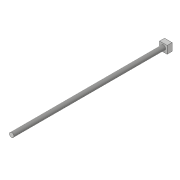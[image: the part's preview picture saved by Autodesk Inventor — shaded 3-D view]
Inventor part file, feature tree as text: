
AUTODESK INVENTOR PART (.ipt)
format: ipt  version: 2019 (Build 230136000, 136)  size: 96,256 bytes
history: native  units: in
note: dims shown in document units (in); Inventor stores cm internally (conversion verified against a paired STEP export)
features: extrude x3, sketch x3, thread x2, plane x1
ambient origin geometry x8: Origin, YZ Plane, XZ Plane, XY Plane, X Axis, Y Axis, Z Axis, Center Point
bodies: Solid1 (feature_tree)
feature tree (9):
  extrude  "Extrusion1"  Depth=0.5906in
  extrude  "Extrusion2"  Depth=0.3937in TaperAngle=0.0deg
  thread  "Thread1"  [1 undecoded]
  plane  "Work Plane1"
  extrude  "Extrusion3"  Depth=0.3937in
  thread  "Thread2"  [1 undecoded]
  sketch  "Sketch1"  dims[d0=0.5906in d1=0.5906in]
  sketch  "Sketch2"  dims[d2=0.3937in d3=0.0in d5=9.8425in d6=0.0in d7=0.3937in d8=0.0in]
  sketch  "Sketch3"  dims[d9=0.0in d10=0.3543in d11=1.9685in d12=0.0in d13=0.3937in d14=0.0in d15=0.3543in]
note: 2 required parameter values undecoded (feature->parameter linkage not recoverable at this tier; creation-order binding heuristic only, values carry confidence <= 0.55)
